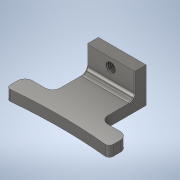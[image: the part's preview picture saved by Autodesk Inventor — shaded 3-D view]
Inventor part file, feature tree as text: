
AUTODESK INVENTOR PART (.ipt)
format: ipt  version: 2020 (Build 240168000, 168)  size: 353,792 bytes
history: native  units: mm
features: fillet x4, sketch x4, extrude x2, projected_geometry x2, hole x1, chamfer x1
ambient origin geometry x8: Origin, YZ Plane, XZ Plane, XY Plane, X Axis, Y Axis, Z Axis, Center Point
bodies: Volumenkörper1 (feature_tree)
feature tree (14):
  extrude  "Extrusion1"  Depth=6.0mm
  hole  "Bohrung1"  [1 undecoded]
  chamfer  "Fase1"  Distance=25.0mm
  fillet  "Rundung1"  Radius=0.5mm
  fillet  "Rundung2"  Radius=1.0mm
  sketch  "Skizze5"  dims[d7=4.917mm d8=12.0mm d9=4.0mm d10=2.0mm d11=90.0deg d12=17.1mm d13=20.594885mm]
  extrude  "Extrusion2"  Depth=3.0mm
  fillet  "Fillet3"  Radius=10.0mm
  fillet  "Fillet4"  Radius=24.0mm
  sketch  "Skizze1"  dims[d0=18.5mm d1=6.0mm]
  sketch  "Skizze2"  dims[d2=5.5mm d3=24.0mm d4=25.0mm d5=0.0mm]
  projected_geometry  "Projizierte Kontur1"
  projected_geometry  "Projizierte Kontur4"
  sketch  "Sketch7"  dims[d14=2.0mm d15=2.0mm d16=45.0deg d38=0.5mm d39=1.0mm d44=54.0mm d45=10.0mm d46=24.0mm d47=250.0mm d48=25.0mm d49=0.0mm d50=2.0mm d51=4.0mm d52=3.0mm]
note: 1 required parameter value undecoded (feature->parameter linkage not recoverable at this tier; creation-order binding heuristic only, values carry confidence <= 0.55)
